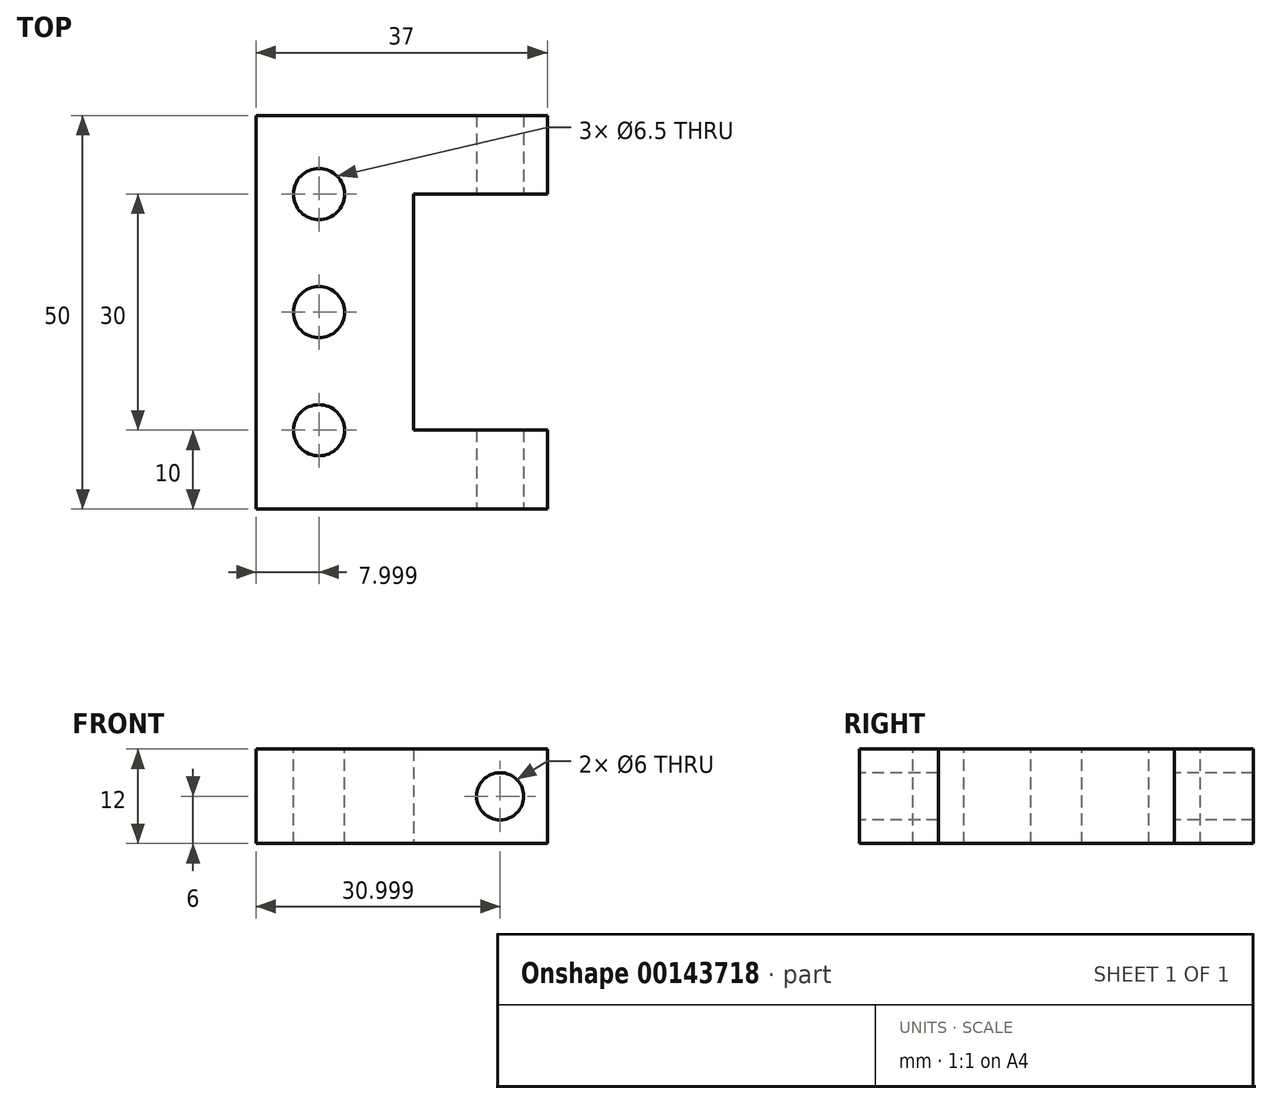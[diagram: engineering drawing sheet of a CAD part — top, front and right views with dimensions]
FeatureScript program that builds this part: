
annotation { "Feature Type Name" : "Feature", "Feature Type Description" : "" }
export const myFeature = defineFeature(function(context is Context, id is Id, definition is map)
    precondition{}
    {
        {
            var Q0;
            Q0=qCreatedBy(makeId("Top.planeOp"),FACE);
            var sketch = newSketch(context, id + "F0", { "sketchPlane" : qUnion([Q0])});
            skLineSegment(sketch, "E0", {"start": v(-25.71, 0) * mm, "end": v(-25.71, 25) * mm});
            skLineSegment(sketch, "E1", {"start": v(-25.71, 25) * mm, "end": v(11.29, 25) * mm});
            skLineSegment(sketch, "E2", {"start": v(11.29, 25) * mm, "end": v(11.29, 15) * mm});
            skLineSegment(sketch, "E3", {"start": v(11.29, 15) * mm, "end": v(-5.71, 15) * mm});
            skLineSegment(sketch, "E4", {"start": v(-5.71, 15) * mm, "end": v(-5.71, 0) * mm});
            skLineSegment(sketch, "E5.MirrorCS", {"start": v(11.29, -15) * mm, "end": v(-5.71, -15) * mm});
            skLineSegment(sketch, "E6.MirrorCS", {"start": v(11.29, -25) * mm, "end": v(11.29, -15) * mm});
            skLineSegment(sketch, "E7.MirrorCS", {"start": v(-25.71, -25) * mm, "end": v(11.29, -25) * mm});
            skLineSegment(sketch, "E8.MirrorCS", {"start": v(-25.71, 0) * mm, "end": v(-25.71, -25) * mm});
            skLineSegment(sketch, "E9.MirrorCS", {"start": v(-5.71, -15) * mm, "end": v(-5.71, 0) * mm});
            skSolve(sketch);
        }
        {
            var Q0;
            Q0 = qSketchRegion(id + "F0", true);
            extrude(context, id + "F1", {"entities" : qUnion([Q0]), "depth" : 12 * mm});
        }
        {
            var Q0;
            Q0=makeQuery(id+"F1.opExtrude","CAP_FACE",FACE,{"disambiguationData":[OSD([sQuery(id+"F0.wireOp",EDGE,"E0"),sQuery(id+"F0.wireOp",EDGE,"E1"),sQuery(id+"F0.wireOp",EDGE,"E2"),sQuery(id+"F0.wireOp",EDGE,"E3"),sQuery(id+"F0.wireOp",EDGE,"E4"),sQuery(id+"F0.wireOp",EDGE,"E5.MirrorCS"),sQuery(id+"F0.wireOp",EDGE,"E6.MirrorCS"),sQuery(id+"F0.wireOp",EDGE,"E7.MirrorCS"),sQuery(id+"F0.wireOp",EDGE,"E8.MirrorCS"),sQuery(id+"F0.wireOp",EDGE,"E9.MirrorCS")])],"isStart":false});
            var sketch = newSketch(context, id + "F2", { "sketchPlane" : qUnion([Q0])});
            skLineSegment(sketch, "E10", {"start": v(-17.71, -42.23) * mm, "end": v(-17.71, 43.96) * mm, "construction": true});
            skPoint(sketch, "E11", {"position": v(-17.71, 0) * mm});
            skPoint(sketch, "E12", {"position": v(-17.71, 15) * mm});
            skPoint(sketch, "E13", {"position": v(-17.71, -15) * mm});
            skSolve(sketch);
        }
        {
            var Q0;
            Q0=sQuery(id+"F2.wireOp",VERTEX,"E13");
            var Q1;
            Q1=sQuery(id+"F2.wireOp",VERTEX,"E11");
            var Q2;
            Q2=sQuery(id+"F2.wireOp",VERTEX,"E12");
            var Q3;
            Q3=makeQuery(id+"F1.opExtrude","SWEPT_BODY",BODY,{"disambiguationData":[OSD([sQuery(id+"F0.wireOp",EDGE,"E0"),sQuery(id+"F0.wireOp",EDGE,"E1"),sQuery(id+"F0.wireOp",EDGE,"E2"),sQuery(id+"F0.wireOp",EDGE,"E3"),sQuery(id+"F0.wireOp",EDGE,"E4"),sQuery(id+"F0.wireOp",EDGE,"E5.MirrorCS"),sQuery(id+"F0.wireOp",EDGE,"E6.MirrorCS"),sQuery(id+"F0.wireOp",EDGE,"E7.MirrorCS"),sQuery(id+"F0.wireOp",EDGE,"E8.MirrorCS"),sQuery(id+"F0.wireOp",EDGE,"E9.MirrorCS")])]});
            hole(context, id + "F3", {"style" : HoleStyle.SIMPLE, "endStyle" : HoleEndStyle.THROUGH, "holeDiameter" : 6.5 * mm, "locations" : qUnion([Q0, Q1, Q2]), "scope" : qUnion([Q3]), "isTappedThrough" : true});
        }
        {
            var Q0;
            Q0=makeQuery(id+"F1.opExtrude","SWEPT_FACE",FACE,{"disambiguationData":[OSD([sQuery(id+"F0.wireOp",EDGE,"E7.MirrorCS")])]});
            var sketch = newSketch(context, id + "F4", { "sketchPlane" : qUnion([Q0])});
            skPoint(sketch, "E14", {"position": v(5.29, 6) * mm});
            skSolve(sketch);
        }
        {
            var Q0;
            Q0=sQuery(id+"F4.wireOp",VERTEX,"E14");
            var Q1;
            Q1=makeQuery(id+"F1.opExtrude","SWEPT_BODY",BODY,{"disambiguationData":[OSD([sQuery(id+"F0.wireOp",EDGE,"E0"),sQuery(id+"F0.wireOp",EDGE,"E1"),sQuery(id+"F0.wireOp",EDGE,"E2"),sQuery(id+"F0.wireOp",EDGE,"E3"),sQuery(id+"F0.wireOp",EDGE,"E4"),sQuery(id+"F0.wireOp",EDGE,"E5.MirrorCS"),sQuery(id+"F0.wireOp",EDGE,"E6.MirrorCS"),sQuery(id+"F0.wireOp",EDGE,"E7.MirrorCS"),sQuery(id+"F0.wireOp",EDGE,"E8.MirrorCS"),sQuery(id+"F0.wireOp",EDGE,"E9.MirrorCS")])]});
            hole(context, id + "F5", {"style" : HoleStyle.SIMPLE, "endStyle" : HoleEndStyle.THROUGH, "holeDiameter" : 6 * mm, "locations" : qUnion([Q0]), "scope" : qUnion([Q1]), "isTappedThrough" : true});
        }
    });
